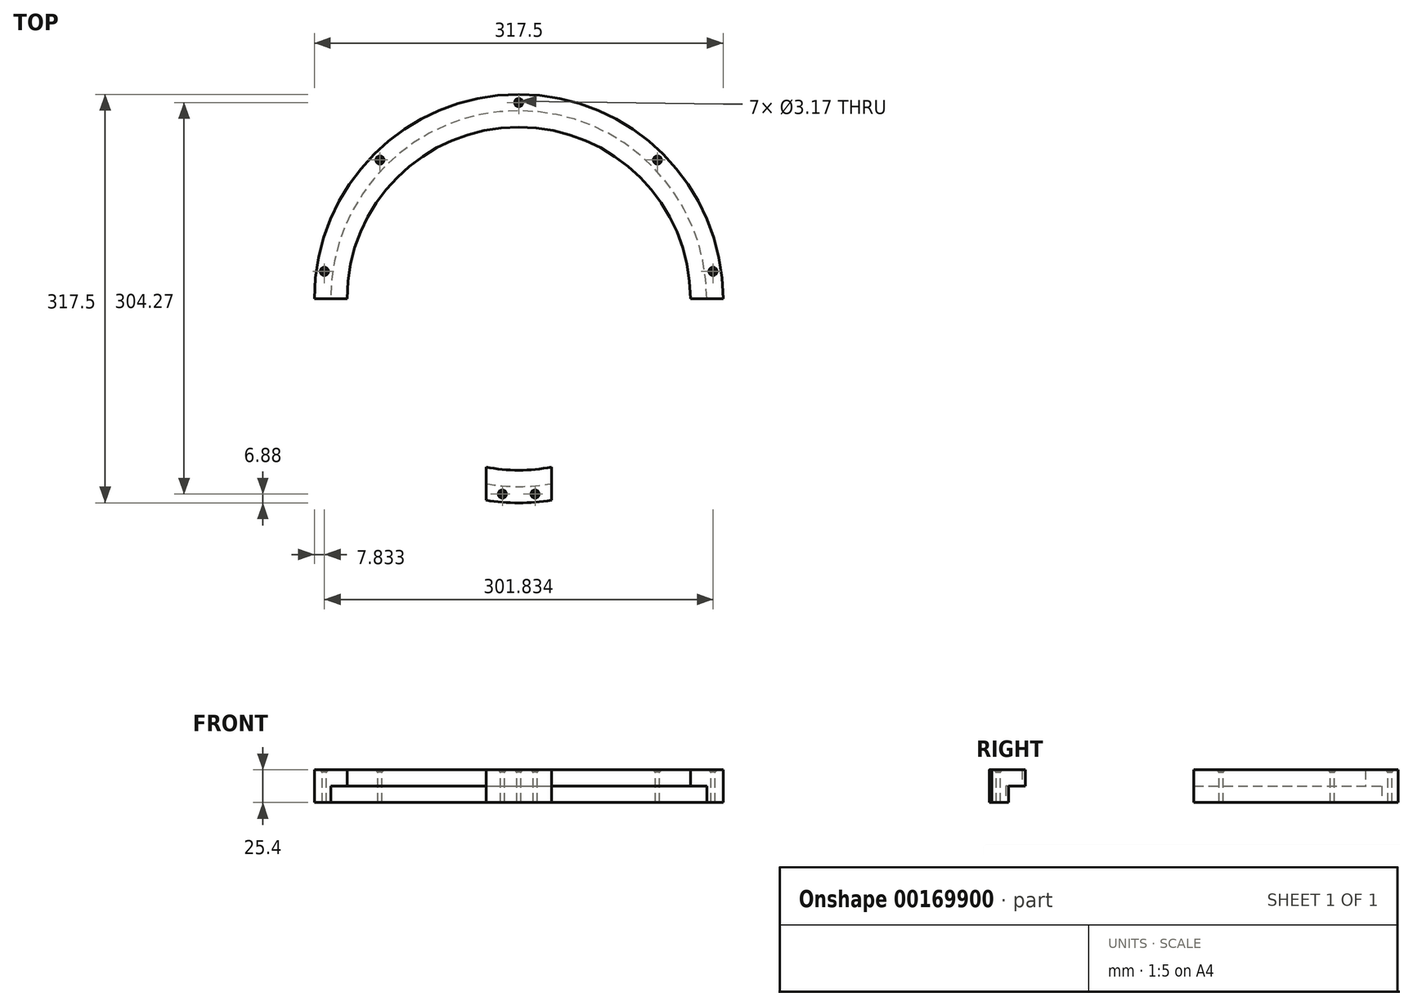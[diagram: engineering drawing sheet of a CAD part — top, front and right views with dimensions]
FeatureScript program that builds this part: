
annotation { "Feature Type Name" : "Feature", "Feature Type Description" : "" }
export const myFeature = defineFeature(function(context is Context, id is Id, definition is map)
    precondition{}
    {
        {
            var Q0;
            Q0=qCreatedBy(makeId("Top.planeOp"),FACE);
            var sketch = newSketch(context, id + "F0", { "sketchPlane" : qUnion([Q0])});
            skCircle(sketch, "E0", {"center": v(0, 0) * mm, "radius": 133.35 * mm});
            skCircle(sketch, "E1", {"center": v(0, 0) * mm, "radius": 158.75 * mm});
            skSolve(sketch);
        }
        {
            var Q0;
            Q0 = qSketchRegion(id + "F0", true);
            extrude(context, id + "F1", {"entities" : qUnion([Q0]), "depth" : 25.4 * mm});
        }
        {
            var Q0;
            Q0=makeQuery(id+"F1.opExtrude","CAP_FACE",FACE,{"disambiguationData":[OSD([sQuery(id+"F0.wireOp",EDGE,"E0"),sQuery(id+"F0.wireOp",EDGE,"E1")])],"isStart":true});
            var sketch = newSketch(context, id + "F2", { "sketchPlane" : qUnion([Q0])});
            skCircle(sketch, "E2", {"center": v(0, 0) * mm, "radius": 146.05 * mm});
            skCircle(sketch, "E3", {"center": v(0, 0) * mm, "radius": 133.35 * mm});
            skSolve(sketch);
        }
        {
            var Q0;
            Q0 = qSketchRegion(id + "F2", true);
            extrude(context, id + "F3", {"entities" : qUnion([Q0]), "operationType" : NewBodyOperationType.REMOVE, "oppositeDirection" : true, "depth" : 12.7 * mm});
        }
        {
            var Q0;
            Q0=makeQuery(id+"F1.opExtrude","CAP_FACE",FACE,{"disambiguationData":[OSD([sQuery(id+"F0.wireOp",EDGE,"E0"),sQuery(id+"F0.wireOp",EDGE,"E1")])],"isStart":false});
            var sketch = newSketch(context, id + "F4", { "sketchPlane" : qUnion([Q0])});
            skLineSegment(sketch, "E4", {"start": v(133.35, 0) * mm, "end": v(158.75, 0) * mm});
            skLineSegment(sketch, "E5", {"start": v(-133.35, 0) * mm, "end": v(-158.75, 0) * mm});
            skLineSegment(sketch, "E6", {"start": v(-25.4, -130.9) * mm, "end": v(-25.4, -156.7) * mm});
            skLineSegment(sketch, "E7", {"start": v(25.4, -156.7) * mm, "end": v(25.4, -130.9) * mm});
            skArc(sketch, "E8", {"start": v(-133.35, 0) * mm, "mid": v(-102.88, -84.84) * mm, "end": v(-25.4, -130.9) * mm});
            skArc(sketch, "E9", {"start": v(-158.75, 0) * mm, "mid": v(-120.9, -102.88) * mm, "end": v(-25.4, -156.7) * mm});
            skArc(sketch, "E10", {"start": v(25.4, -130.9) * mm, "mid": v(102.88, -84.84) * mm, "end": v(133.35, 0) * mm});
            skArc(sketch, "E11", {"start": v(158.75, 0) * mm, "mid": v(120.9, -102.88) * mm, "end": v(25.4, -156.7) * mm});
            skSolve(sketch);
        }
        {
            var Q0;
            Q0 = qSketchRegion(id + "F4", true);
            extrude(context, id + "F5", {"entities" : qUnion([Q0]), "operationType" : NewBodyOperationType.REMOVE, "endBound" : BoundingType.THROUGH_ALL, "oppositeDirection" : true, "depth" : 25.4 * mm});
        }
        {
            var Q0;
            {var subQ0=sQuery(id+"F0.wireOp",EDGE,"E0");var subQ1=sQuery(id+"F0.wireOp",EDGE,"E1");Q0=makeQuery(id+"F5.boolean.opBoolean","SPLIT",FACE,{"disambiguationData":[TD([makeQuery(id+"F5.opExtrude","SWEPT_FACE",FACE,{"disambiguationData":[OSD([sQuery(id+"F4.wireOp",EDGE,"E4")])]})])],"derivedFrom":makeQuery(id+"F1.opExtrude","CAP_FACE",FACE,{"disambiguationData":[OSD([subQ0,subQ1])],"isStart":false})});}
            var sketch = newSketch(context, id + "F6", { "sketchPlane" : qUnion([Q0])});
            skCircle(sketch, "E12", {"center": v(0, 0) * mm, "radius": 152.4 * mm});
            skPoint(sketch, "E13", {"position": v(0, 152.4) * mm});
            skPoint(sketch, "E14", {"position": v(-107.76, 107.76) * mm});
            skPoint(sketch, "E15", {"position": v(-150.92, 21.2) * mm});
            skPoint(sketch, "E16", {"position": v(150.92, 21.2) * mm});
            skPoint(sketch, "E17", {"position": v(107.76, 107.76) * mm});
            skPoint(sketch, "E18", {"position": v(-12.7, -151.87) * mm});
            skPoint(sketch, "E19", {"position": v(12.7, -151.87) * mm});
            skSolve(sketch);
        }
        {
            var Q0;
            Q0=sQuery(id+"F6.wireOp",VERTEX,"E15");
            var Q1;
            Q1=sQuery(id+"F6.wireOp",VERTEX,"E14");
            var Q2;
            Q2=sQuery(id+"F6.wireOp",VERTEX,"E13");
            var Q3;
            Q3=sQuery(id+"F6.wireOp",VERTEX,"E17");
            var Q4;
            Q4=sQuery(id+"F6.wireOp",VERTEX,"E16");
            var Q5;
            Q5=sQuery(id+"F6.wireOp",VERTEX,"E18");
            var Q6;
            Q6=sQuery(id+"F6.wireOp",VERTEX,"E19");
            var Q7;
            Q7=makeQuery(id+"F5.boolean.opBoolean","SPLIT",BODY,{"disambiguationData":[OD(0.0)],"derivedFrom":makeQuery(id+"F1.opExtrude","SWEPT_BODY",BODY,{"disambiguationData":[OSD([sQuery(id+"F0.wireOp",EDGE,"E0"),sQuery(id+"F0.wireOp",EDGE,"E1")])]})});
            var Q8;
            Q8=makeQuery(id+"F5.boolean.opBoolean","SPLIT",BODY,{"disambiguationData":[OD(1.0)],"derivedFrom":makeQuery(id+"F1.opExtrude","SWEPT_BODY",BODY,{"disambiguationData":[OSD([sQuery(id+"F0.wireOp",EDGE,"E0"),sQuery(id+"F0.wireOp",EDGE,"E1")])]})});
            hole(context, id + "F7", {"style" : HoleStyle.C_SINK, "endStyle" : HoleEndStyle.BLIND, "holeDiameter" : 3.17 * mm, "cSinkDiameter" : 6.35 * mm, "cSinkAngle" : 82 * degree, "holeDepth" : 31.75 * mm, "startFromSketch" : true, "locations" : qUnion([Q0, Q1, Q2, Q3, Q4, Q5, Q6]), "scope" : qUnion([Q7, Q8])});
        }
    });
